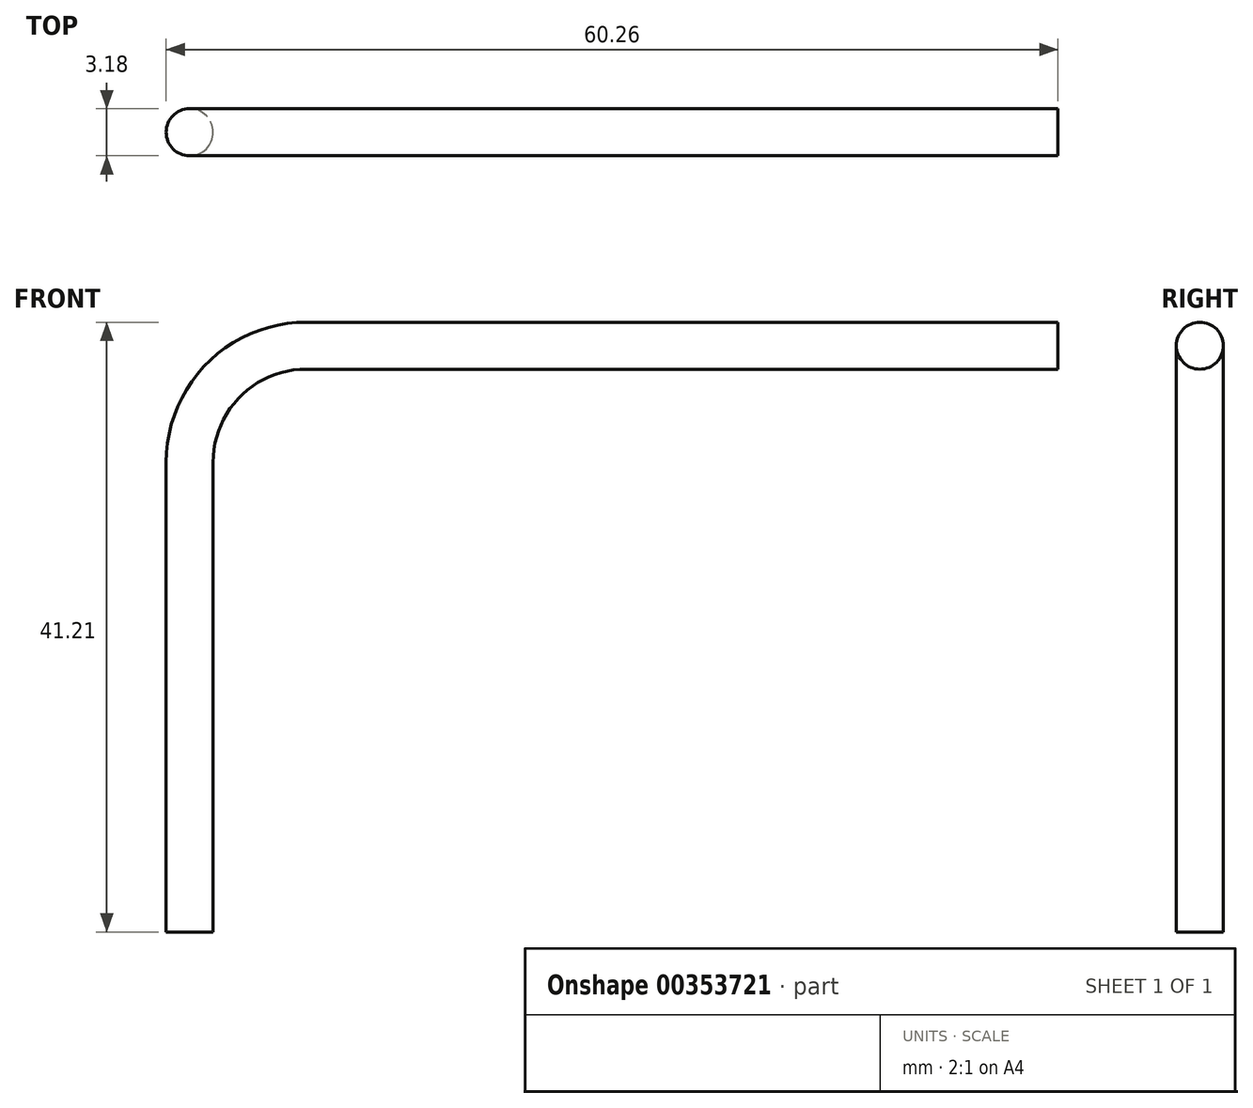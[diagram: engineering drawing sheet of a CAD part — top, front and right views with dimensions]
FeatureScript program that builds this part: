
annotation { "Feature Type Name" : "Feature", "Feature Type Description" : "" }
export const myFeature = defineFeature(function(context is Context, id is Id, definition is map)
    precondition{}
    {
        {
            var Q0;
            Q0=qCreatedBy(makeId("Top.planeOp"),FACE);
            var sketch = newSketch(context, id + "F0", { "sketchPlane" : qUnion([Q0])});
            skCircle(sketch, "E0", {"center": v(0, 0) * mm, "radius": 1.59 * mm});
            skSolve(sketch);
        }
        {
            var Q0;
            Q0=qCreatedBy(makeId("Front.planeOp"),FACE);
            var sketch = newSketch(context, id + "F1", { "sketchPlane" : qUnion([Q0])});
            skLineSegment(sketch, "E1", {"start": v(0, 0) * mm, "end": v(0, 31.75) * mm});
            skLineSegment(sketch, "E2", {"start": v(7.87, 39.62) * mm, "end": v(58.67, 39.62) * mm});
            skPoint(sketch, "E3.visualSharp", {"position": v(0, 39.62) * mm});
            skArc(sketch, "E3.filletArc", {"start": v(7.87, 39.62) * mm, "mid": v(2.3, 37.32) * mm, "end": v(0, 31.75) * mm});
            skSolve(sketch);
        }
        {
            var Q0;
            Q0 = qSketchRegion(id + "F0", true);
            var Q1;
            Q1 = qConstructionFilter(qBodyType(qCreatedBy(id + "F1" ,EDGE), BodyType.WIRE), ConstructionObject.NO);
            sweep(context, id + "F2", {"profiles" : qUnion([Q0]), "path" : qUnion([Q1])});
        }
    });
